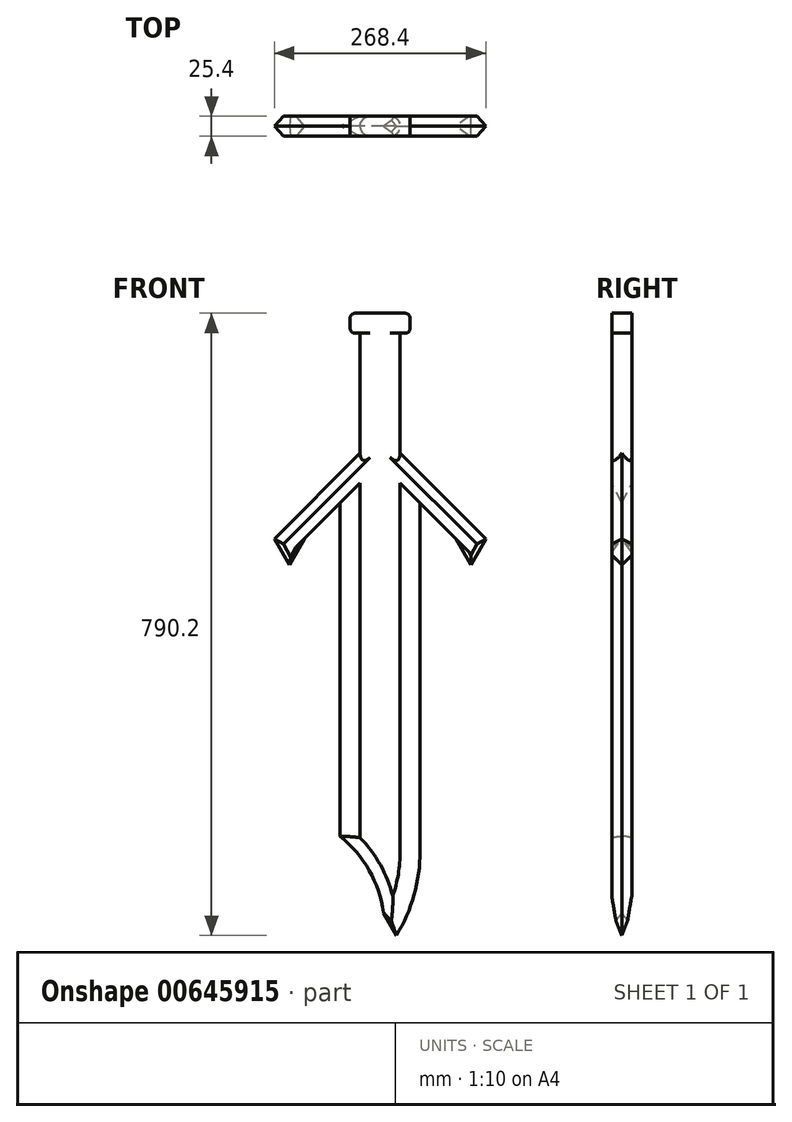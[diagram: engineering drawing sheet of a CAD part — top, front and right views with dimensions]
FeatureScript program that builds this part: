
annotation { "Feature Type Name" : "Feature", "Feature Type Description" : "" }
export const myFeature = defineFeature(function(context is Context, id is Id, definition is map)
    precondition{}
    {
        {
            var Q0;
            Q0=qCreatedBy(makeId("Front.planeOp"),FACE);
            var sketch = newSketch(context, id + "F0", { "sketchPlane" : qUnion([Q0])});
            skLineSegment(sketch, "E0", {"start": v(12.7, 61.35) * mm, "end": v(12.7, 48.65) * mm});
            skLineSegment(sketch, "E1", {"start": v(19.05, 42.3) * mm, "end": v(82.55, 42.3) * mm});
            skLineSegment(sketch, "E2", {"start": v(88.9, 48.65) * mm, "end": v(88.9, 61.35) * mm});
            skLineSegment(sketch, "E3", {"start": v(82.55, 67.7) * mm, "end": v(19.05, 67.7) * mm});
            skLineSegment(sketch, "E4", {"start": v(25.4, 42.3) * mm, "end": v(25.4, -110.1) * mm});
            skLineSegment(sketch, "E5", {"start": v(25.4, -110.1) * mm, "end": v(76.2, -110.1) * mm});
            skLineSegment(sketch, "E6", {"start": v(76.2, -110.1) * mm, "end": v(76.2, 42.3) * mm});
            skPoint(sketch, "E7.visualSharp", {"position": v(88.9, 42.3) * mm});
            skArc(sketch, "E7.filletArc", {"start": v(82.55, 42.3) * mm, "mid": v(87.04, 44.16) * mm, "end": v(88.9, 48.65) * mm});
            skPoint(sketch, "E8.visualSharp", {"position": v(12.7, 42.3) * mm});
            skArc(sketch, "E8.filletArc", {"start": v(12.7, 48.65) * mm, "mid": v(14.56, 44.16) * mm, "end": v(19.05, 42.3) * mm});
            skPoint(sketch, "E9.visualSharp", {"position": v(88.9, 67.7) * mm});
            skArc(sketch, "E9.filletArc", {"start": v(88.9, 61.35) * mm, "mid": v(87.04, 65.84) * mm, "end": v(82.55, 67.7) * mm});
            skPoint(sketch, "E10.visualSharp", {"position": v(12.7, 67.7) * mm});
            skArc(sketch, "E10.filletArc", {"start": v(19.05, 67.7) * mm, "mid": v(14.56, 65.84) * mm, "end": v(12.7, 61.35) * mm});
            skLineSegment(sketch, "E11", {"start": v(25.4, -110.1) * mm, "end": v(-83.4, -218.9) * mm});
            skLineSegment(sketch, "E12", {"start": v(-45.3, -218.9) * mm, "end": v(25.4, -148.2) * mm});
            skLineSegment(sketch, "E13", {"start": v(25.4, -148.2) * mm, "end": v(76.2, -148.2) * mm});
            skLineSegment(sketch, "E14", {"start": v(76.2, -148.2) * mm, "end": v(146.9, -218.9) * mm});
            skLineSegment(sketch, "E15", {"start": v(185, -218.9) * mm, "end": v(76.2, -110.1) * mm});
            skCircle(sketch, "E16.cCircle", {"center": v(50.8, -192.2) * mm, "radius": 44 * mm, "construction": true});
            skPoint(sketch, "E16.cCircle.centerSnap0", {"position": v(50.8, -148.2) * mm});
            skLineSegment(sketch, "E16.1", {"start": v(76.2, -148.2) * mm, "end": v(101.6, -192.2) * mm});
            skLineSegment(sketch, "E16.2", {"start": v(101.6, -192.2) * mm, "end": v(76.2, -236.19) * mm});
            skLineSegment(sketch, "E16.3", {"start": v(76.2, -236.19) * mm, "end": v(25.4, -236.19) * mm});
            skLineSegment(sketch, "E16.4", {"start": v(25.4, -236.19) * mm, "end": v(0, -192.2) * mm});
            skLineSegment(sketch, "E16.5", {"start": v(0, -192.2) * mm, "end": v(25.4, -148.2) * mm});
            skPoint(sketch, "E16.0.midPoint", {"position": v(50.8, -148.2) * mm});
            skCircle(sketch, "E17", {"center": v(50.8, -192.2) * mm, "radius": 31.75 * mm});
            skPoint(sketch, "E18.endSnap0", {"position": v(50.8, -236.19) * mm});
            skPoint(sketch, "E19.endSnap0", {"position": v(88.9, -170.2) * mm});
            skLineSegment(sketch, "E20", {"start": v(0, -173.6) * mm, "end": v(0, -598.7) * mm});
            skLineSegment(sketch, "E21", {"start": v(52.73, -690.04) * mm, "end": v(71.47, -722.5) * mm});
            skLineSegment(sketch, "E22", {"start": v(101.6, -616.03) * mm, "end": v(101.6, -173.6) * mm});
            skLineSegment(sketch, "E23", {"start": v(185, -218.9) * mm, "end": v(165.95, -251.9) * mm});
            skLineSegment(sketch, "E24", {"start": v(165.95, -251.9) * mm, "end": v(146.9, -218.9) * mm});
            skLineSegment(sketch, "E25", {"start": v(-45.3, -218.9) * mm, "end": v(-64.35, -251.9) * mm});
            skLineSegment(sketch, "E26", {"start": v(-64.35, -251.9) * mm, "end": v(-83.4, -218.9) * mm});
            skPoint(sketch, "E27.visualSharp", {"position": v(0, -598.7) * mm});
            skPoint(sketch, "E28.visualSharp", {"position": v(101.6, -738.5) * mm});
            skArc(sketch, "E28.filletArc", {"start": v(71.47, -722.5) * mm, "mid": v(93.92, -671.36) * mm, "end": v(101.6, -616.03) * mm});
            skPoint(sketch, "E29.visualSharp", {"position": v(84.83, -745.63) * mm});
            skArc(sketch, "E30", {"start": v(52.73, -690.04) * mm, "mid": v(34.87, -639.46) * mm, "end": v(0, -598.7) * mm});
            skSolve(sketch);
        }
        {
            var Q0;
            Q0=makeQuery(id+"F0.imprint","IMPRINT",FACE,{"disambiguationData":[TD([[makeQuery(id+"F0.imprint","IMPRINT",EDGE,{"derivedFrom":sQuery(id+"F0.wireOp",EDGE,"E0")}),1.0]])]});
            var Q1;
            {var subQ3=sQuery(id+"F0.wireOp",EDGE,"E16.2");Q1=makeQuery(id+"F0.imprint","IMPRINT",FACE,{"disambiguationData":[TD([[makeQuery(id+"F0.imprint","IMPRINT",EDGE,{"derivedFrom":subQ3}),1.0]])]});}
            var Q2;
            {var subQ0=sQuery(id+"F0.wireOp",EDGE,"E4");Q2=makeQuery(id+"F0.imprint","IMPRINT",FACE,{"disambiguationData":[TD([[makeQuery(id+"F0.imprint","IMPRINT",EDGE,{"derivedFrom":subQ0}),1.0]])]});}
            var Q3;
            Q3=makeQuery(id+"F0.imprint","IMPRINT",FACE,{"disambiguationData":[TD([[makeQuery(id+"F0.imprint","IMPRINT",EDGE,{"derivedFrom":sQuery(id+"F0.wireOp",EDGE,"E5")}),-1.0]])]});
            var Q4;
            Q4=makeQuery(id+"F0.imprint","IMPRINT",FACE,{"disambiguationData":[TD([[makeQuery(id+"F0.imprint","IMPRINT",EDGE,{"derivedFrom":sQuery(id+"F0.wireOp",EDGE,"E13")}),-1.0]])]});
            var Q5;
            Q5=makeQuery(id+"F0.imprint","IMPRINT",FACE,{"disambiguationData":[TD([[makeQuery(id+"F0.imprint","IMPRINT",EDGE,{"derivedFrom":sQuery(id+"F0.wireOp",EDGE,"E17")}),1.0]])]});
            var Q6;
            {var subQ0=sQuery(id+"F0.wireOp",EDGE,"E16.5");Q6=makeQuery(id+"F0.imprint","IMPRINT",FACE,{"disambiguationData":[TD([[makeQuery(id+"F0.imprint","IMPRINT",EDGE,{"derivedFrom":subQ0}),1.0]])]});}
            var Q7;
            {var subQ0=sQuery(id+"F0.wireOp",EDGE,"E16.1");Q7=makeQuery(id+"F0.imprint","IMPRINT",FACE,{"disambiguationData":[TD([[makeQuery(id+"F0.imprint","IMPRINT",EDGE,{"derivedFrom":subQ0}),1.0]])]});}
            extrude(context, id + "F1", {"entities" : qUnion([Q0, Q1, Q2, Q3, Q4, Q5, Q6, Q7]), "depth" : 25.4 * mm, "offsetDistance" : 25.4 * mm});
        }
        {
            var Q0;
            Q0=makeQuery(id+"F1.opExtrude","CAP_EDGE",EDGE,{"disambiguationData":[OSD([sQuery(id+"F0.wireOp",EDGE,"E20")])],"isStart":false});
            var Q1;
            Q1=makeQuery(id+"F1.opExtrude","CAP_EDGE",EDGE,{"disambiguationData":[OSD([sQuery(id+"F0.wireOp",EDGE,"E20")])],"isStart":true});
            chamfer(context, id + "F2", {"entities" : qUnion([Q0, Q1]), "chamferType" : ChamferType.TWO_OFFSETS, "width1" : 25.4 * mm, "oppositeDirection" : false, "width2" : 12.7 * mm, "tangentPropagation" : true});
        }
        {
            var Q0;
            Q0=makeQuery(id+"F1.opExtrude","CAP_EDGE",EDGE,{"disambiguationData":[OSD([sQuery(id+"F0.wireOp",EDGE,"E30")])],"isStart":false});
            var Q1;
            Q1=makeQuery(id+"F1.opExtrude","CAP_EDGE",EDGE,{"disambiguationData":[OSD([sQuery(id+"F0.wireOp",EDGE,"E30")])],"isStart":true});
            chamfer(context, id + "F3", {"entities" : qUnion([Q0, Q1]), "chamferType" : ChamferType.TWO_OFFSETS, "width1" : 17.27 * mm, "oppositeDirection" : true, "width2" : 13.97 * mm, "tangentPropagation" : true});
        }
        {
            var Q0;
            Q0=makeQuery(id+"F1.opExtrude","CAP_EDGE",EDGE,{"disambiguationData":[OSD([sQuery(id+"F0.wireOp",EDGE,"E21")])],"isStart":false});
            var Q1;
            Q1=makeQuery(id+"F1.opExtrude","CAP_EDGE",EDGE,{"disambiguationData":[OSD([sQuery(id+"F0.wireOp",EDGE,"E21")])],"isStart":true});
            chamfer(context, id + "F4", {"entities" : qUnion([Q0, Q1]), "chamferType" : ChamferType.TWO_OFFSETS, "width1" : 6.35 * mm, "oppositeDirection" : false, "width2" : 12.7 * mm, "tangentPropagation" : true});
        }
        {
            var Q0;
            Q0=makeQuery(id+"F1.opExtrude","CAP_EDGE",EDGE,{"disambiguationData":[OSD([sQuery(id+"F0.wireOp",EDGE,"E28.filletArc")])],"isStart":true});
            var Q1;
            Q1=makeQuery(id+"F1.opExtrude","CAP_EDGE",EDGE,{"disambiguationData":[OSD([sQuery(id+"F0.wireOp",EDGE,"E28.filletArc")])],"isStart":false});
            chamfer(context, id + "F5", {"entities" : qUnion([Q0, Q1]), "chamferType" : ChamferType.TWO_OFFSETS, "width1" : 12.7 * mm, "oppositeDirection" : false, "width2" : 25.4 * mm, "tangentPropagation" : true});
        }
        {
            var Q0;
            Q0=makeQuery(id+"F1.opExtrude","CAP_EDGE",EDGE,{"disambiguationData":[OSD([sQuery(id+"F0.wireOp",EDGE,"E26")])],"isStart":false});
            var Q1;
            Q1=makeQuery(id+"F1.opExtrude","CAP_EDGE",EDGE,{"disambiguationData":[OSD([sQuery(id+"F0.wireOp",EDGE,"E26")])],"isStart":true});
            chamfer(context, id + "F6", {"entities" : qUnion([Q0, Q1]), "chamferType" : ChamferType.TWO_OFFSETS, "width1" : 12.7 * mm, "oppositeDirection" : false, "width2" : 6.35 * mm, "tangentPropagation" : true});
        }
        {
            var Q0;
            Q0=makeQuery(id+"F1.opExtrude","CAP_EDGE",EDGE,{"disambiguationData":[OSD([sQuery(id+"F0.wireOp",EDGE,"E23")])],"isStart":false});
            var Q1;
            Q1=makeQuery(id+"F1.opExtrude","CAP_EDGE",EDGE,{"disambiguationData":[OSD([sQuery(id+"F0.wireOp",EDGE,"E23")])],"isStart":true});
            chamfer(context, id + "F7", {"entities" : qUnion([Q0, Q1]), "chamferType" : ChamferType.TWO_OFFSETS, "width1" : 12.7 * mm, "oppositeDirection" : false, "width2" : 6.35 * mm, "tangentPropagation" : true});
        }
        {
            var Q0;
            Q0=makeQuery(id+"F1.opExtrude","CAP_EDGE",EDGE,{"disambiguationData":[OSD([sQuery(id+"F0.wireOp",EDGE,"E25")])],"isStart":true});
            var Q1;
            Q1=makeQuery(id+"F1.opExtrude","CAP_EDGE",EDGE,{"disambiguationData":[OSD([sQuery(id+"F0.wireOp",EDGE,"E25")])],"isStart":false});
            chamfer(context, id + "F8", {"entities" : qUnion([Q0, Q1]), "chamferType" : ChamferType.TWO_OFFSETS, "width1" : 3.8 * mm, "oppositeDirection" : false, "width2" : 12.7 * mm, "tangentPropagation" : true});
        }
        {
            var Q0;
            Q0=makeQuery(id+"F1.opExtrude","CAP_EDGE",EDGE,{"disambiguationData":[OSD([sQuery(id+"F0.wireOp",EDGE,"E24")])],"isStart":false});
            var Q1;
            Q1=makeQuery(id+"F1.opExtrude","CAP_EDGE",EDGE,{"disambiguationData":[OSD([sQuery(id+"F0.wireOp",EDGE,"E24")])],"isStart":true});
            chamfer(context, id + "F9", {"entities" : qUnion([Q0, Q1]), "chamferType" : ChamferType.TWO_OFFSETS, "width1" : 12.7 * mm, "oppositeDirection" : false, "width2" : 6.35 * mm, "tangentPropagation" : true});
        }
        {
            var Q0;
            Q0=makeQuery(id+"F1.opExtrude","CAP_EDGE",EDGE,{"disambiguationData":[OSD([sQuery(id+"F0.wireOp",EDGE,"E11")])],"isStart":true});
            var Q1;
            Q1=makeQuery(id+"F1.opExtrude","CAP_EDGE",EDGE,{"disambiguationData":[OSD([sQuery(id+"F0.wireOp",EDGE,"E11")])],"isStart":false});
            var Q2;
            Q2=makeQuery(id+"F1.opExtrude","CAP_EDGE",EDGE,{"disambiguationData":[OSD([sQuery(id+"F0.wireOp",EDGE,"E15")])],"isStart":false});
            var Q3;
            Q3=makeQuery(id+"F1.opExtrude","CAP_EDGE",EDGE,{"disambiguationData":[OSD([sQuery(id+"F0.wireOp",EDGE,"E15")])],"isStart":true});
            chamfer(context, id + "F10", {"entities" : qUnion([Q0, Q1, Q2, Q3]), "chamferType" : ChamferType.TWO_OFFSETS, "width1" : 12.7 * mm, "oppositeDirection" : false, "width2" : 12.7 * mm, "tangentPropagation" : true});
        }
        {
            var Q0;
            Q0=makeQuery(id+"F1.opExtrude","CAP_EDGE",EDGE,{"disambiguationData":[OSD([sQuery(id+"F0.wireOp",EDGE,"E6")])],"isStart":false});
            var Q1;
            Q1=makeQuery(id+"F1.opExtrude","CAP_EDGE",EDGE,{"disambiguationData":[OSD([sQuery(id+"F0.wireOp",EDGE,"E6")])],"isStart":true});
            var Q2;
            Q2=makeQuery(id+"F1.opExtrude","CAP_EDGE",EDGE,{"disambiguationData":[OSD([sQuery(id+"F0.wireOp",EDGE,"E4")])],"isStart":false});
            var Q3;
            Q3=makeQuery(id+"F1.opExtrude","CAP_EDGE",EDGE,{"disambiguationData":[OSD([sQuery(id+"F0.wireOp",EDGE,"E4")])],"isStart":true});
            fillet(context, id + "F11", {"entities" : qUnion([Q0, Q1, Q2, Q3]), "radius" : 12.7 * mm, "tangentPropagation" : true, "allowEdgeOverflow" : false});
        }
    });
